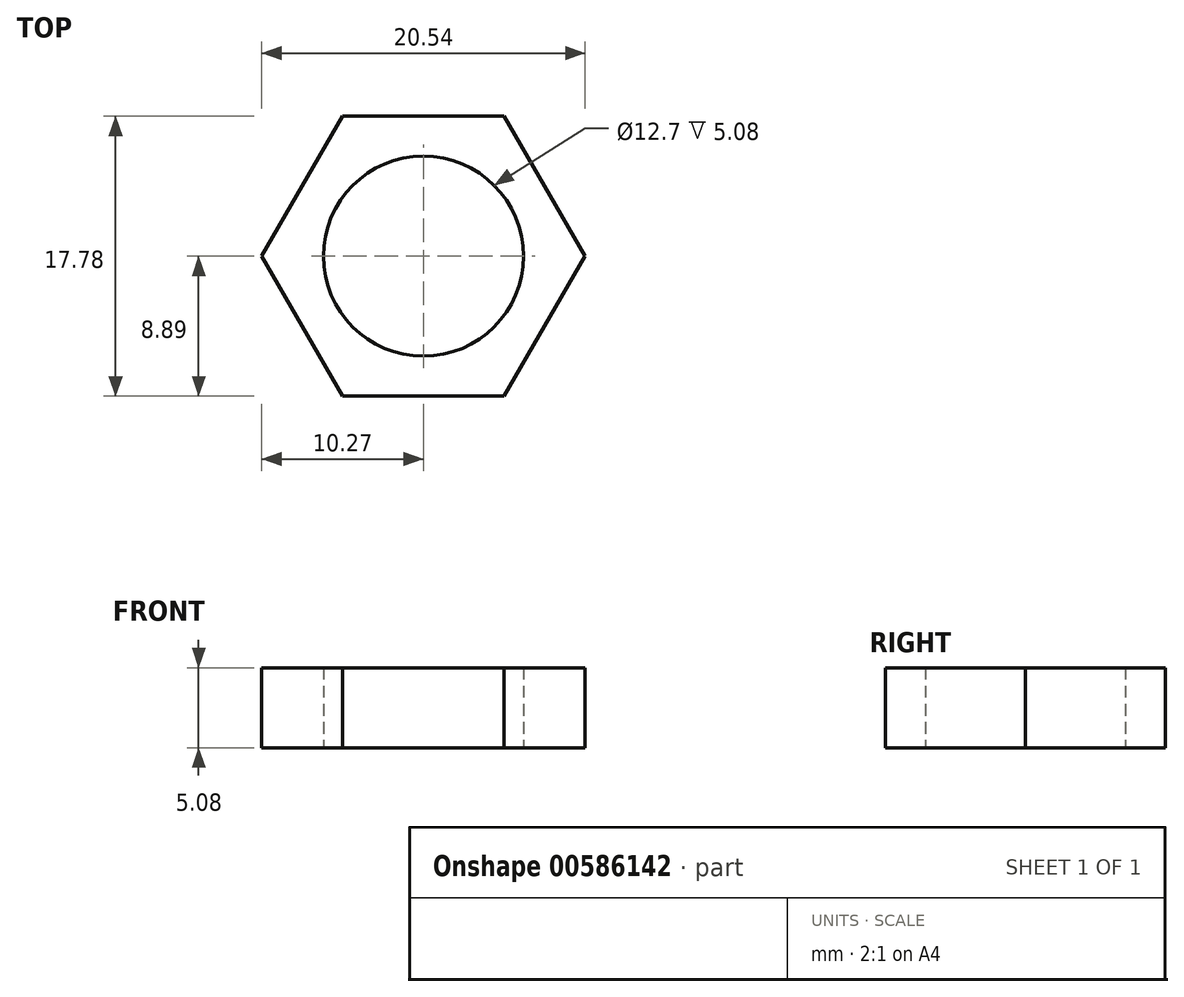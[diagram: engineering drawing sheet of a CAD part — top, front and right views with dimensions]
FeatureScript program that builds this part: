
annotation { "Feature Type Name" : "Feature", "Feature Type Description" : "" }
export const myFeature = defineFeature(function(context is Context, id is Id, definition is map)
    precondition{}
    {
        {
            var Q0;
            Q0=qCreatedBy(makeId("Top.planeOp"),FACE);
            var sketch = newSketch(context, id + "F0", { "sketchPlane" : qUnion([Q0])});
            skCircle(sketch, "E0", {"center": v(0, 0) * mm, "radius": 6.35 * mm});
            skCircle(sketch, "E1.cCircle", {"center": v(0, 0) * mm, "radius": 8.9 * mm, "construction": true});
            skLineSegment(sketch, "E1.0", {"start": v(5.13, -8.9) * mm, "end": v(-5.13, -8.9) * mm});
            skLineSegment(sketch, "E1.1", {"start": v(-5.13, -8.9) * mm, "end": v(-10.27, 0) * mm});
            skLineSegment(sketch, "E1.2", {"start": v(-10.27, 0) * mm, "end": v(-5.13, 8.89) * mm});
            skLineSegment(sketch, "E1.3", {"start": v(-5.13, 8.9) * mm, "end": v(5.13, 8.9) * mm});
            skLineSegment(sketch, "E1.4", {"start": v(5.13, 8.9) * mm, "end": v(10.27, 0) * mm});
            skLineSegment(sketch, "E1.5", {"start": v(10.27, 0) * mm, "end": v(5.13, -8.9) * mm});
            skPoint(sketch, "E1.0.midPoint", {"position": v(0, -8.9) * mm});
            skSolve(sketch);
        }
        {
            var Q0;
            Q0=makeQuery(id+"F0.imprint","IMPRINT",FACE,{"disambiguationData":[TD([[makeQuery(id+"F0.imprint","IMPRINT",EDGE,{"derivedFrom":sQuery(id+"F0.wireOp",EDGE,"E0")}),-1.0]])]});
            extrude(context, id + "F1", {"entities" : qUnion([Q0]), "depth" : 5.08 * mm, "offsetDistance" : 25.4 * mm});
        }
    });
